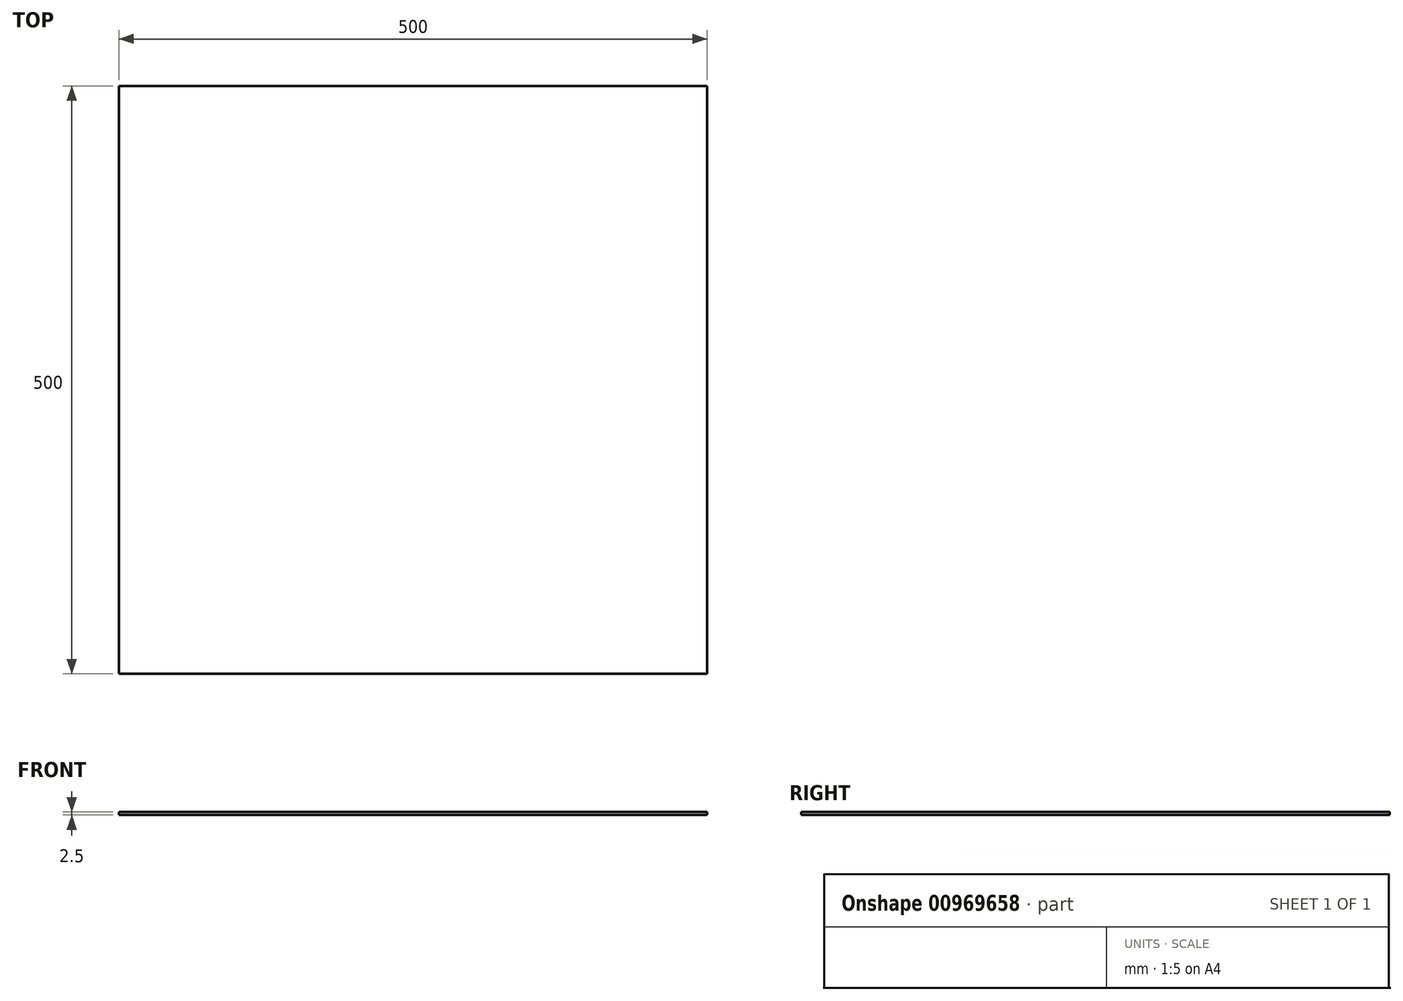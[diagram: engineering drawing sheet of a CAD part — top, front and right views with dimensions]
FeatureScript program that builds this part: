
annotation { "Feature Type Name" : "Feature", "Feature Type Description" : "" }
export const myFeature = defineFeature(function(context is Context, id is Id, definition is map)
    precondition{}
    {
        {
            assignVariable(context, id + "F0", {"name" : "glass_W", "anyValue" : 2.5});
        }
        {
            var Q0;
            Q0=qCreatedBy(makeId("Top.planeOp"),FACE);
            var sketch = newSketch(context, id + "F1", { "sketchPlane" : qUnion([Q0])});
            skLineSegment(sketch, "E0.bottom", {"start": v(-250, 250) * mm, "end": v(250, 250) * mm});
            skLineSegment(sketch, "E0.top", {"start": v(-250, -250) * mm, "end": v(250, -250) * mm});
            skLineSegment(sketch, "E0.left", {"start": v(-250, 250) * mm, "end": v(-250, -250) * mm});
            skLineSegment(sketch, "E0.right", {"start": v(250, 250) * mm, "end": v(250, -250) * mm});
            skPoint(sketch, "E0.middle", {"position": v(0, 0) * mm});
            skSolve(sketch);
        }
        {
            var Q0;
            Q0=makeQuery(id+"F1.imprint","IMPRINT",FACE,{"disambiguationData":[TD([[makeQuery(id+"F1.imprint","IMPRINT",EDGE,{"derivedFrom":sQuery(id+"F1.wireOp",EDGE,"E0.bottom")}),-1.0]])]});
            extrude(context, id + "F2", {"entities" : qUnion([Q0]), "depth" : (getVariable(context, 'glass_W')) * mm, "offsetDistance" : 25 * mm});
        }
    });
